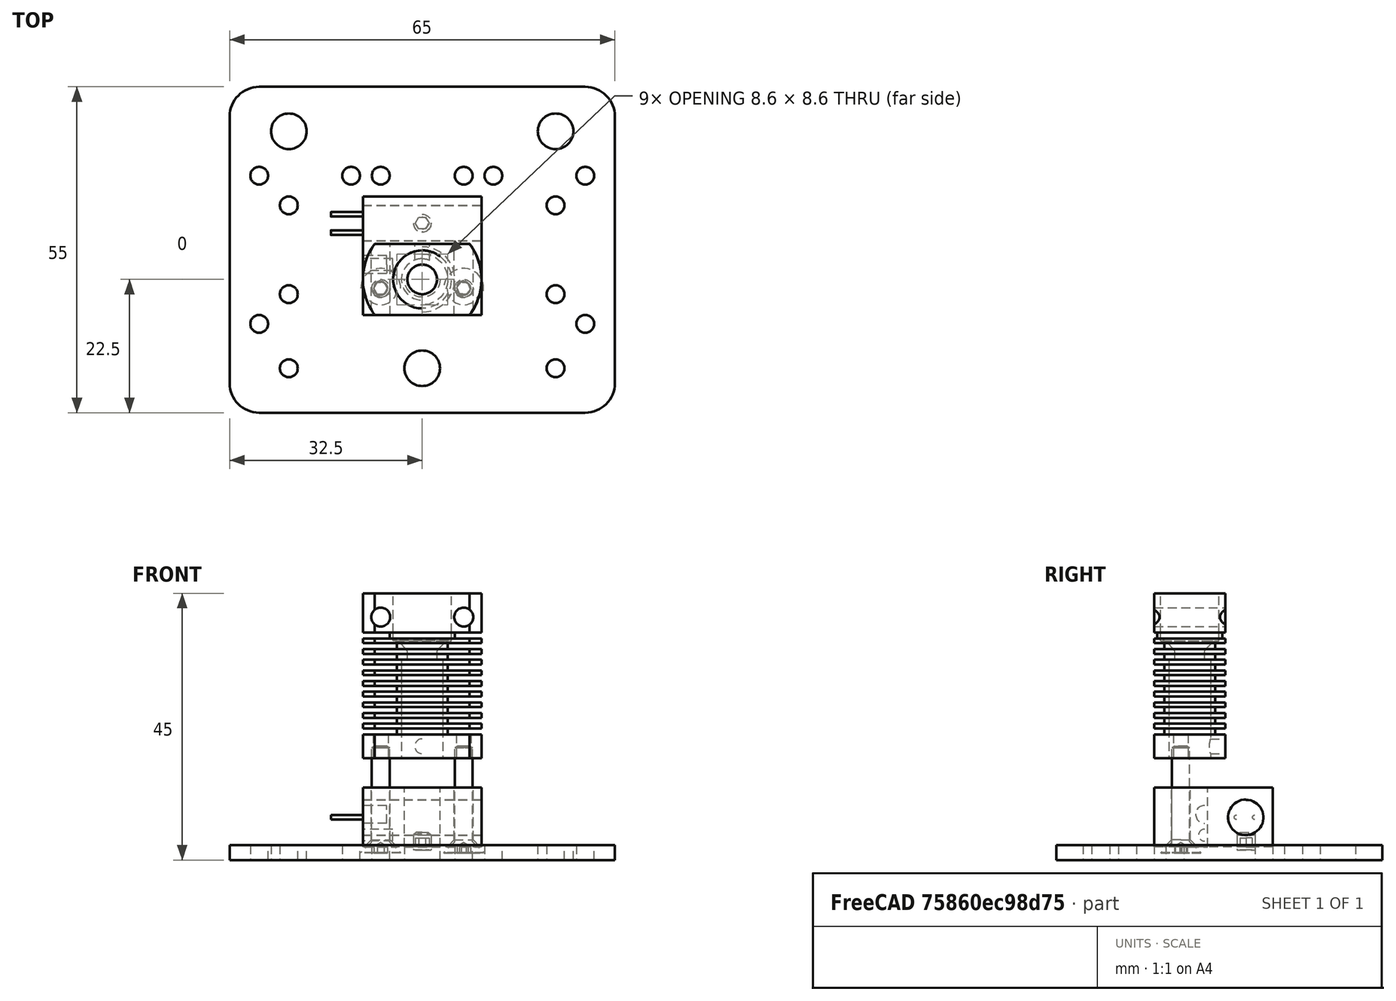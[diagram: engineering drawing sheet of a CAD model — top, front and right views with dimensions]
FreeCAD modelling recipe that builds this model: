
FCSTD DOCUMENT  (FreeCAD 0.19R24276 (Git))
Label: assembly_v1
License: All rights reserved
LicenseURL: http://en.wikipedia.org/wiki/All_rights_reserved
objects: App::FeaturePython×37, Part::FeaturePython×31, Part::Feature×7
note: 37 computed .brp shape members not serialized (recipe doc carries the construction recipe); baked Part::Feature solids carry a one-line shape summary decoded from their .brp

FEATURE [Part::Feature] Part__Feature  label="Heat block"
  Placement = pos=(2.95042e-06,-1.00001,2.2) rot=(-0.577355,-0.577345,0.577351;0rad)
  shape: bbox 20 x 20 x 10 mm, 26 faces (baked)
FEATURE [Part::Feature] Part__Feature001  label="Heater"
  Placement = pos=(-10,4.49999,7.2) rot=(0,1,0;1.5708rad)
  shape: bbox 25.42 x 5.9 x 5.9 mm, 10 faces (baked)
FEATURE [Part::Feature] Part__Feature002  label="Radiator"
  Placement = pos=(8.76188e-07,-5,41) rot=(-0.707107,-0.707107,0;3.14159rad)
  shape: bbox 20 x 12 x 27.8 mm, 110 faces (baked)
FEATURE [Part::Feature] Part__Feature003  label="HotendPlate"
  shape: bbox 65 x 55 x 2.5 mm, 27 faces (baked)
FEATURE [Part::Feature] Part__Feature004  label="blockScreww"
  Placement = pos=(-7,-6.50001,19.2) rot=(-0.577678,-0.576695,-0.577678;2.09538rad)
  shape: bbox 6.721 x 6.721 x 18 mm, 27 faces (baked)
FEATURE [Part::Feature] Part__Feature006  label="blockScrew02"
  Placement = pos=(7,-6.5,19.2) rot=(-0.602638,-0.523121,-0.602638;2.17765rad)
  shape: bbox 6.721 x 6.721 x 18 mm, 27 faces (baked)
FEATURE [Part::Feature] Part__Feature007  label="M3 Screw"
  Placement = pos=(2.65241e-06,4.49999,1.7) rot=(1,0,0;1.5708rad)
  shape: bbox 3 x 3 x 3 mm, 13 faces (baked)
FEATURE [Part::FeaturePython] Parts  # WARN: FeaturePython — macro-defined, semantics opaque (R4)
  Group = -> [Origin,Part__Feature003,Part__Feature,Part__Feature001,Part__Feature002,Part__Feature004,Part__Feature006,Part__Feature007]
  GroupMode = 0
FEATURE [Part::FeaturePython] Assembly  # WARN: FeaturePython — macro-defined, semantics opaque (R4)
  AutoRelax = true
  BuildShape = 0
  Freeze = false
  Group = -> [Constraints,Elements,Parts]
  Verbose = false
  _SolverType = 1
  _Version = 1
FEATURE [App::FeaturePython] Constraints  # WARN: FeaturePython — macro-defined, semantics opaque (R4)
  Group = -> [Constraint,Constraint003,Constraint004,Constraint005,Constraint006,Constraint007,Constraint008,Constraint009,Constraint010,Constraint011,Constraint012,Constraint013]
  _Version = 1
FEATURE [App::FeaturePython] Elements  # WARN: FeaturePython — macro-defined, semantics opaque (R4)
  Group = -> [_Element,_Element001,_Element002,_Element003,_Element004,_Element005,_Element006,_Element007,_Element008,_Element009,_Element010,_Element011,_Element012,_Element013,_Element014,_Element015,_Element016,_Element017,_Element018,_Element019,_Element020,_Element021,_Element022,_Element023,_Element024,_Element025,_Element026,_Element027,_Element028]
FEATURE [Part::FeaturePython] _Element  # link proxy (typed FeaturePython)
  Detach = false
  LinkTransform = true
  LinkedObject = -> Part__Feature002 [Face46]
  _Parent = -> Elements
FEATURE [Part::FeaturePython] _Element001  # link proxy (typed FeaturePython)
  Detach = false
  LinkTransform = true
  LinkedObject = -> Part__Feature [Edge37]
  _Parent = -> Elements
FEATURE [Part::FeaturePython] _Element002  # link proxy (typed FeaturePython)
  Detach = false
  LinkTransform = true
  LinkedObject = -> Part__Feature002 [Edge20]
  _Parent = -> Elements
FEATURE [Part::FeaturePython] _Element003  # link proxy (typed FeaturePython)
  Detach = false
  LinkTransform = true
  LinkedObject = -> Part__Feature [Edge6]
  _Parent = -> Elements
FEATURE [Part::FeaturePython] _Element004  # link proxy (typed FeaturePython)
  Detach = false
  LinkTransform = true
  LinkedObject = -> Part__Feature002 [Edge101]
  _Parent = -> Elements
FEATURE [Part::FeaturePython] _Element005  # link proxy (typed FeaturePython)
  Detach = false
  LinkTransform = true
  LinkedObject = -> Part__Feature [Edge2]
  _Parent = -> Elements
FEATURE [Part::FeaturePython] _Element006  # link proxy (typed FeaturePython)
  Detach = false
  LinkTransform = true
  LinkedObject = -> Part__Feature [Edge36]
  _Parent = -> Elements
FEATURE [Part::FeaturePython] _Element007  # link proxy (typed FeaturePython)
  Detach = false
  LinkTransform = true
  LinkedObject = -> Part__Feature002 [Edge100]
  _Parent = -> Elements
FEATURE [Part::FeaturePython] _Element008  # link proxy (typed FeaturePython)
  Detach = false
  LinkTransform = true
  LinkedObject = -> Part__Feature002 [Edge16]
  _Parent = -> Elements
FEATURE [App::FeaturePython] Constraint  label="Locked"  # WARN: FeaturePython — macro-defined, semantics opaque (R4)
  Disabled = false
  Group = -> [ElementLink]
  _ConstraintType = 0
  _Parent = -> Constraints
FEATURE [App::FeaturePython] ElementLink  label="_Element"  # link proxy (typed FeaturePython)
  LinkTransform = true
  LinkedObject = -> _Element
  _Parent = -> Constraint
FEATURE [Part::FeaturePython] _Element009  # link proxy (typed FeaturePython)
  Detach = false
  LinkTransform = true
  LinkedObject = -> Part__Feature004 [Face27]
  _Parent = -> Elements
FEATURE [Part::FeaturePython] _Element010  # link proxy (typed FeaturePython)
  Detach = false
  LinkTransform = true
  LinkedObject = -> Part__Feature006 [Face27]
  _Parent = -> Elements
FEATURE [App::FeaturePython] Constraint003  label="AxialAlignment002"  # WARN: FeaturePython — macro-defined, semantics opaque (R4)
  Angle = 0
  AnglePitch = 0
  AngleRoll = 0
  Disabled = false
  Group = -> [ElementLink005,ElementLink006]
  LockAngle = false
  Multiply = false
  _ConstraintType = 36
  _Parent = -> Constraints
FEATURE [App::FeaturePython] ElementLink005  label="_Element009"  # link proxy (typed FeaturePython)
  LinkTransform = true
  LinkedObject = -> _Element009
  _Parent = -> Constraint003
FEATURE [App::FeaturePython] ElementLink006  label="_Element008"  # link proxy (typed FeaturePython)
  LinkTransform = true
  LinkedObject = -> _Element008
  _Parent = -> Constraint003
FEATURE [App::FeaturePython] Constraint004  label="AxialAlignment003"  # WARN: FeaturePython — macro-defined, semantics opaque (R4)
  Angle = 0
  AnglePitch = 0
  AngleRoll = 0
  Disabled = false
  Group = -> [ElementLink007,ElementLink008]
  LockAngle = false
  Multiply = false
  _ConstraintType = 36
  _Parent = -> Constraints
FEATURE [App::FeaturePython] ElementLink007  label="_Element002"  # link proxy (typed FeaturePython)
  LinkTransform = true
  LinkedObject = -> _Element002
  _Parent = -> Constraint004
FEATURE [App::FeaturePython] ElementLink008  label="_Element010"  # link proxy (typed FeaturePython)
  LinkTransform = true
  LinkedObject = -> _Element010
  _Parent = -> Constraint004
FEATURE [Part::FeaturePython] _Element011  # link proxy (typed FeaturePython)
  Detach = false
  LinkTransform = true
  LinkedObject = -> Part__Feature004 [Edge27]
  _Parent = -> Elements
FEATURE [Part::FeaturePython] _Element012  # link proxy (typed FeaturePython)
  Detach = false
  LinkTransform = true
  LinkedObject = -> Part__Feature [Edge43]
  _Parent = -> Elements
FEATURE [Part::FeaturePython] _Element013  # link proxy (typed FeaturePython)
  Detach = false
  LinkTransform = true
  LinkedObject = -> Part__Feature006 [Edge27]
  _Parent = -> Elements
FEATURE [Part::FeaturePython] _Element014  # link proxy (typed FeaturePython)
  Detach = false
  LinkTransform = true
  LinkedObject = -> Part__Feature [Edge44]
  _Parent = -> Elements
FEATURE [Part::FeaturePython] _Element015  # link proxy (typed FeaturePython)
  Detach = false
  LinkTransform = true
  LinkedObject = -> Part__Feature004 [Edge20]
  _Parent = -> Elements
FEATURE [Part::FeaturePython] _Element016  # link proxy (typed FeaturePython)
  Detach = false
  LinkTransform = true
  LinkedObject = -> Part__Feature006 [Edge20]
  _Parent = -> Elements
FEATURE [App::FeaturePython] Constraint005  label="AxialAlignment"  # WARN: FeaturePython — macro-defined, semantics opaque (R4)
  Angle = 0
  AnglePitch = 0
  AngleRoll = 0
  Disabled = false
  Group = -> [ElementLink009,ElementLink010]
  LockAngle = false
  Multiply = false
  _ConstraintType = 36
  _Parent = -> Constraints
FEATURE [App::FeaturePython] ElementLink009  label="_Element009"  # link proxy (typed FeaturePython)
  LinkTransform = true
  LinkedObject = -> _Element009
  _Parent = -> Constraint005
FEATURE [App::FeaturePython] ElementLink010  label="_Element005"  # link proxy (typed FeaturePython)
  LinkTransform = true
  LinkedObject = -> _Element005
  _Parent = -> Constraint005
FEATURE [App::FeaturePython] Constraint006  label="AxialAlignment004"  # WARN: FeaturePython — macro-defined, semantics opaque (R4)
  Angle = 0
  AnglePitch = 0
  AngleRoll = 0
  Disabled = false
  Group = -> [ElementLink011,ElementLink012]
  LockAngle = false
  Multiply = false
  _ConstraintType = 36
  _Parent = -> Constraints
FEATURE [App::FeaturePython] ElementLink011  label="_Element010"  # link proxy (typed FeaturePython)
  LinkTransform = true
  LinkedObject = -> _Element010
  _Parent = -> Constraint006
FEATURE [App::FeaturePython] ElementLink012  label="_Element001"  # link proxy (typed FeaturePython)
  LinkTransform = true
  LinkedObject = -> _Element001
  _Parent = -> Constraint006
FEATURE [App::FeaturePython] Constraint007  label="PointsPlaneDistance"  # WARN: FeaturePython — macro-defined, semantics opaque (R4)
  Disabled = false
  Distance = -1
  Group = -> [ElementLink013,ElementLink014]
  _ConstraintType = 7
  _Parent = -> Constraints
FEATURE [App::FeaturePython] ElementLink013  label="_Element017"  # link proxy (typed FeaturePython)
  LinkTransform = true
  LinkedObject = -> _Element017
  _Parent = -> Constraint007
FEATURE [Part::FeaturePython] _Element017  # link proxy (typed FeaturePython)
  Detach = false
  LinkTransform = true
  LinkedObject = -> Part__Feature004 [Edge24]
  _Parent = -> Elements
FEATURE [App::FeaturePython] ElementLink014  label="_Element018"  # link proxy (typed FeaturePython)
  LinkTransform = true
  LinkedObject = -> _Element018
  _Parent = -> Constraint007
FEATURE [Part::FeaturePython] _Element018  # link proxy (typed FeaturePython)
  Detach = false
  LinkTransform = true
  LinkedObject = -> Part__Feature [Face20]
  _Parent = -> Elements
FEATURE [App::FeaturePython] Constraint008  label="PointsPlaneDistance001"  # WARN: FeaturePython — macro-defined, semantics opaque (R4)
  Disabled = false
  Distance = 1
  Group = -> [ElementLink015,ElementLink016]
  _ConstraintType = 7
  _Parent = -> Constraints
FEATURE [App::FeaturePython] ElementLink015  label="_Element018"  # link proxy (typed FeaturePython)
  LinkTransform = true
  LinkedObject = -> _Element018
  _Parent = -> Constraint008
FEATURE [App::FeaturePython] ElementLink016  label="_Element019"  # link proxy (typed FeaturePython)
  LinkTransform = true
  LinkedObject = -> _Element019
  _Parent = -> Constraint008
FEATURE [Part::FeaturePython] _Element019  # link proxy (typed FeaturePython)
  Detach = false
  LinkTransform = true
  LinkedObject = -> Part__Feature006 [Edge24]
  _Parent = -> Elements
FEATURE [Part::FeaturePython] _Element020  # link proxy (typed FeaturePython)
  Detach = false
  LinkTransform = true
  LinkedObject = -> Part__Feature007 [Face4]
  _Parent = -> Elements
FEATURE [App::FeaturePython] Constraint009  label="AxialAlignment005"  # WARN: FeaturePython — macro-defined, semantics opaque (R4)
  Angle = 0
  AnglePitch = 0
  AngleRoll = 0
  Disabled = false
  Group = -> [ElementLink017,ElementLink018]
  LockAngle = false
  Multiply = false
  _ConstraintType = 36
  _Parent = -> Constraints
FEATURE [App::FeaturePython] ElementLink017  label="_Element021"  # link proxy (typed FeaturePython)
  LinkTransform = true
  LinkedObject = -> _Element021
  _Parent = -> Constraint009
FEATURE [Part::FeaturePython] _Element021  # link proxy (typed FeaturePython)
  Detach = false
  LinkTransform = true
  LinkedObject = -> Part__Feature [Edge60]
  _Parent = -> Elements
FEATURE [App::FeaturePython] ElementLink018  label="_Element020"  # link proxy (typed FeaturePython)
  LinkTransform = true
  LinkedObject = -> _Element020
  _Parent = -> Constraint009
FEATURE [App::FeaturePython] Constraint010  label="PointsPlaneDistance002"  # WARN: FeaturePython — macro-defined, semantics opaque (R4)
  Disabled = false
  Distance = 0.5
  Group = -> [ElementLink019,ElementLink020]
  _ConstraintType = 7
  _Parent = -> Constraints
FEATURE [App::FeaturePython] ElementLink019  label="_Element018"  # link proxy (typed FeaturePython)
  LinkTransform = true
  LinkedObject = -> _Element018
  _Parent = -> Constraint010
FEATURE [App::FeaturePython] ElementLink020  label="_Element022"  # link proxy (typed FeaturePython)
  LinkTransform = true
  LinkedObject = -> _Element022
  _Parent = -> Constraint010
FEATURE [Part::FeaturePython] _Element022  # link proxy (typed FeaturePython)
  Detach = false
  LinkTransform = true
  LinkedObject = -> Part__Feature007 [Edge9]
  _Parent = -> Elements
FEATURE [App::FeaturePython] Constraint011  label="AxialAlignment006"  # WARN: FeaturePython — macro-defined, semantics opaque (R4)
  Angle = 0
  AnglePitch = 0
  AngleRoll = 0
  Disabled = false
  Group = -> [ElementLink021,ElementLink022]
  LockAngle = false
  Multiply = false
  _ConstraintType = 36
  _Parent = -> Constraints
FEATURE [App::FeaturePython] ElementLink021  label="_Element023"  # link proxy (typed FeaturePython)
  LinkTransform = true
  LinkedObject = -> _Element023
  _Parent = -> Constraint011
FEATURE [Part::FeaturePython] _Element023  # link proxy (typed FeaturePython)
  Detach = false
  LinkTransform = true
  LinkedObject = -> Part__Feature001 [Face4]
  _Parent = -> Elements
FEATURE [App::FeaturePython] ElementLink022  label="_Element024"  # link proxy (typed FeaturePython)
  LinkTransform = true
  LinkedObject = -> _Element024
  _Parent = -> Constraint011
FEATURE [Part::FeaturePython] _Element024  # link proxy (typed FeaturePython)
  Detach = false
  LinkTransform = true
  LinkedObject = -> Part__Feature [Edge54]
  _Parent = -> Elements
FEATURE [App::FeaturePython] Constraint012  label="PointsPlaneDistance003"  # WARN: FeaturePython — macro-defined, semantics opaque (R4)
  Disabled = false
  Distance = 0
  Group = -> [ElementLink023,ElementLink024]
  _ConstraintType = 7
  _Parent = -> Constraints
FEATURE [App::FeaturePython] ElementLink023  label="_Element025"  # link proxy (typed FeaturePython)
  LinkTransform = true
  LinkedObject = -> _Element025
  _Parent = -> Constraint012
FEATURE [Part::FeaturePython] _Element025  # link proxy (typed FeaturePython)
  Detach = false
  LinkTransform = true
  LinkedObject = -> Part__Feature001 [Edge8]
  _Parent = -> Elements
FEATURE [App::FeaturePython] ElementLink024  label="_Element026"  # link proxy (typed FeaturePython)
  LinkTransform = true
  LinkedObject = -> _Element026
  _Parent = -> Constraint012
FEATURE [Part::FeaturePython] _Element026  # link proxy (typed FeaturePython)
  Detach = false
  LinkTransform = true
  LinkedObject = -> Part__Feature [Face16]
  _Parent = -> Elements
FEATURE [App::FeaturePython] Constraint013  label="PointsPlaneDistance004"  # WARN: FeaturePython — macro-defined, semantics opaque (R4)
  Disabled = false
  Distance = 5
  Group = -> [ElementLink025,ElementLink026]
  _ConstraintType = 7
  _Parent = -> Constraints
FEATURE [App::FeaturePython] ElementLink025  label="_Element027"  # link proxy (typed FeaturePython)
  LinkTransform = true
  LinkedObject = -> _Element027
  _Parent = -> Constraint013
FEATURE [Part::FeaturePython] _Element027  # link proxy (typed FeaturePython)
  Detach = false
  LinkTransform = true
  LinkedObject = -> Part__Feature002 [Face24]
  _Parent = -> Elements
FEATURE [App::FeaturePython] ElementLink026  label="_Element028"  # link proxy (typed FeaturePython)
  LinkTransform = true
  LinkedObject = -> _Element028
  _Parent = -> Constraint013
FEATURE [Part::FeaturePython] _Element028  # link proxy (typed FeaturePython)
  Detach = false
  LinkTransform = true
  LinkedObject = -> Part__Feature [Face10]
  _Parent = -> Elements
